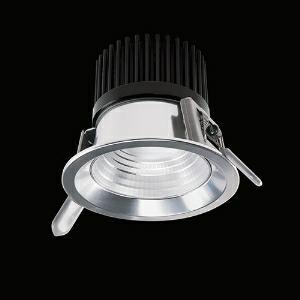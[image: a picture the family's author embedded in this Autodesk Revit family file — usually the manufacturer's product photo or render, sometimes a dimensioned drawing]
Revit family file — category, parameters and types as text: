
# Revit family: spectral_myral_myral_1500-840-f-dali
name_source: partatom
category: Lighting Fixtures
revit_build: Autodesk Revit 2016 (Build: 20150220_1215(x64)
units: mm (PartAtom-declared; Revit-internal decimal feet)

## family parameters
Cut with Voids When Loaded = No
Host = Face
Light Source = No
Part Type = Normal
Room Calculation Point = No
Round Connector Dimension = Use Diameter
Shared = No

## types (1)
- SPECTRAL MYRAL (1 x )
    Apparent Load = 0 VA
    Approval mark = CE
    CIE Flux Codes = 81 99 100 100 100
    Control Gear = Electronic transformer
    Default Elevation = 1800 mm
    Description = SPG0320185
MYRAL recessed spot

Design:
    Height = 0 mm  [stored 0 ft]
    Lamp = 1 x
    Lamp count = 1
    Length = 120 mm
    Luminous efficacy = 0 lm/W
    Manufacturer = Ridi
    ModVariant = No
    Model = MYRAL 1500-840-F-DALI
    Mounting Place = Ceiling
    Mounting Type = Recessed
    Number of Poles = 1
    OnlyDefault = Yes
    Power Factor = 1
    Product Name = SPECTRAL MYRAL
    Product group = Downlight recessed
    ProductGroupID = 400
    Protection Class = Protection class
    Protection Degree = IP 20
    RlxData = <blob elided: 38909 chars, md5=449d8315>
    Socket = socket
    Standby Power = 0 W
    System Light Flux = 0 lm
    System Power = 0 W
    Type Image = myral_04.jpg
    URL = http://reluxnet.relux.com
    VarID = ---
    Voltage = 0 V
    Weight = 0.00 kg
    Width = 0 mm  [stored 0 ft]

note: [stored X ft] marks values corroborated as IEEE doubles in the binary element streams (Revit-internal decimal feet)

## geometry (parser evidence)
native form markers: Sweep x9
no freeform markers — native parametric forms only
